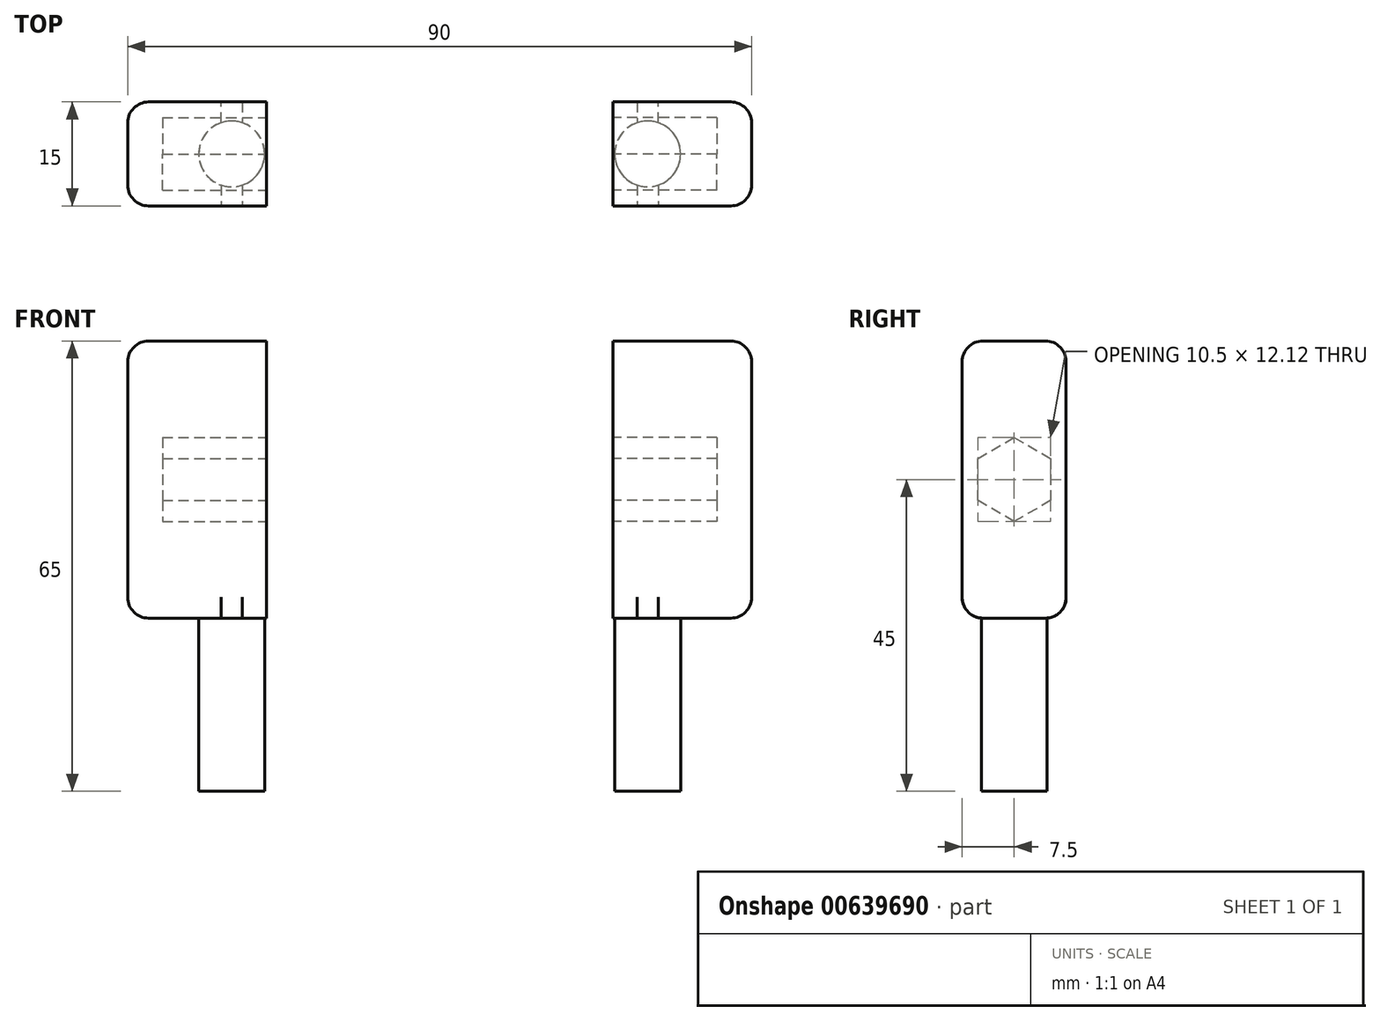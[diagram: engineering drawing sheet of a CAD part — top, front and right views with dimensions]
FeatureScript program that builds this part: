
annotation { "Feature Type Name" : "Feature", "Feature Type Description" : "" }
export const myFeature = defineFeature(function(context is Context, id is Id, definition is map)
    precondition{}
    {
        {
            var Q0;
            Q0=qCreatedBy(makeId("Front.planeOp"),FACE);
            var sketch = newSketch(context, id + "F0", { "sketchPlane" : qUnion([Q0])});
            skLineSegment(sketch, "E0", {"start": v(0, -20) * mm, "end": v(-20, -20) * mm});
            skLineSegment(sketch, "E1", {"start": v(-20, -20) * mm, "end": v(-20, 20) * mm});
            skLineSegment(sketch, "E2", {"start": v(-20, 20) * mm, "end": v(0, 20) * mm});
            skLineSegment(sketch, "E3", {"start": v(0, 20) * mm, "end": v(0, -20) * mm});
            skSolve(sketch);
        }
        {
            var Q0;
            Q0 = qSketchRegion(id + "F0", true);
            extrude(context, id + "F1", {"entities" : qUnion([Q0]), "endBound" : BoundingType.SYMMETRIC, "depth" : 15 * mm, "offsetDistance" : 25 * mm});
        }
        {
            var Q0;
            Q0=qCreatedBy(makeId("Right.planeOp"),FACE);
            var sketch = newSketch(context, id + "F2", { "sketchPlane" : qUnion([Q0])});
            skCircle(sketch, "E4.cCircle", {"center": v(0, 0) * mm, "radius": 5.25 * mm, "construction": true});
            skLineSegment(sketch, "E4.0", {"start": v(5.25, -3.03) * mm, "end": v(0, -6.06) * mm});
            skLineSegment(sketch, "E4.1", {"start": v(0, -6.06) * mm, "end": v(-5.25, -3.03) * mm});
            skLineSegment(sketch, "E4.2", {"start": v(-5.25, -3.03) * mm, "end": v(-5.25, 3.03) * mm});
            skLineSegment(sketch, "E4.3", {"start": v(-5.25, 3.03) * mm, "end": v(0, 6.06) * mm});
            skLineSegment(sketch, "E4.4", {"start": v(0, 6.06) * mm, "end": v(5.25, 3.03) * mm});
            skLineSegment(sketch, "E4.5", {"start": v(5.25, 3.03) * mm, "end": v(5.25, -3.03) * mm});
            skPoint(sketch, "E4.0.midPoint", {"position": v(2.62, -4.55) * mm});
            skSolve(sketch);
        }
        {
            var Q0;
            Q0 = qSketchRegion(id + "F2", true);
            extrude(context, id + "F3", {"entities" : qUnion([Q0]), "operationType" : NewBodyOperationType.REMOVE, "oppositeDirection" : true, "depth" : 15 * mm, "offsetDistance" : 25 * mm});
        }
        {
            var Q0;
            Q0=qCreatedBy(makeId("Top.planeOp"),FACE);
            cPlane(context, id + "F4", {"entities" : qUnion([Q0]), "cplaneType" : CPlaneType.OFFSET, "offset" : 20 * mm, "oppositeDirection" : true, "width" : 150 * mm, "height" : 150 * mm});
        }
        {
            var Q0;
            Q0=qCreatedBy(id+"F4.planeOp",FACE);
            var sketch = newSketch(context, id + "F5", { "sketchPlane" : qUnion([Q0])});
            skCircle(sketch, "E5", {"center": v(-5, 0) * mm, "radius": 4.75 * mm});
            skSolve(sketch);
        }
        {
            var Q0;
            Q0 = qSketchRegion(id + "F5", true);
            extrude(context, id + "F6", {"entities" : qUnion([Q0]), "operationType" : NewBodyOperationType.ADD, "oppositeDirection" : true, "depth" : 25 * mm, "offsetDistance" : 25 * mm});
        }
        {
            var Q0;
            Q0=makeQuery(id+"F1.opExtrude","CAP_EDGE",EDGE,{"disambiguationData":[OSD([sQuery(id+"F0.wireOp",EDGE,"E2")])],"isStart":false});
            var Q1;
            Q1=makeQuery(id+"F1.opExtrude","CAP_EDGE",EDGE,{"disambiguationData":[OSD([sQuery(id+"F0.wireOp",EDGE,"E2")])],"isStart":true});
            var Q2;
            Q2=makeQuery(id+"F1.opExtrude","CAP_EDGE",EDGE,{"disambiguationData":[OSD([sQuery(id+"F0.wireOp",EDGE,"E1")])],"isStart":false});
            var Q3;
            Q3=makeQuery(id+"F1.opExtrude","CAP_EDGE",EDGE,{"disambiguationData":[OSD([sQuery(id+"F0.wireOp",EDGE,"E1")])],"isStart":true});
            var Q4;
            Q4=makeQuery(id+"F1.opExtrude","SWEPT_EDGE",EDGE,{"disambiguationData":[OSD([sQuery(id+"F0.wireOp",EDGE,"E1"),sQuery(id+"F0.wireOp",EDGE,"E2")])]});
            var Q5;
            Q5=makeQuery(id+"F1.opExtrude","CAP_EDGE",EDGE,{"disambiguationData":[OSD([sQuery(id+"F0.wireOp",EDGE,"E0")])],"isStart":true});
            var Q6;
            Q6=makeQuery(id+"F1.opExtrude","CAP_EDGE",EDGE,{"disambiguationData":[OSD([sQuery(id+"F0.wireOp",EDGE,"E0")])],"isStart":false});
            var Q7;
            Q7=makeQuery(id+"F1.opExtrude","SWEPT_EDGE",EDGE,{"disambiguationData":[OSD([sQuery(id+"F0.wireOp",EDGE,"E0"),sQuery(id+"F0.wireOp",EDGE,"E1")])]});
            fillet(context, id + "F7", {"entities" : qUnion([Q0, Q1, Q2, Q3, Q4, Q5, Q6, Q7]), "radius" : 3 * mm, "tangentPropagation" : true, "allowEdgeOverflow" : false});
        }
        {
            var Q0;
            Q0=qCreatedBy(makeId("Right.planeOp"),FACE);
            cPlane(context, id + "F8", {"entities" : qUnion([Q0]), "cplaneType" : CPlaneType.OFFSET, "offset" : 25 * mm, "width" : 150 * mm, "height" : 150 * mm});
        }
        {
            var Q0;
            Q0=makeQuery(id+"F1.opExtrude","SWEPT_BODY",BODY,{"disambiguationData":[OSD([sQuery(id+"F0.wireOp",EDGE,"E0"),sQuery(id+"F0.wireOp",EDGE,"E1"),sQuery(id+"F0.wireOp",EDGE,"E2"),sQuery(id+"F0.wireOp",EDGE,"E3")])]});
            var Q1;
            Q1=qCreatedBy(id+"F8.planeOp",FACE);
            mirror(context, id + "F9", {"entities" : qUnion([Q0]), "mirrorPlane" : qUnion([Q1])});
        }
    });
